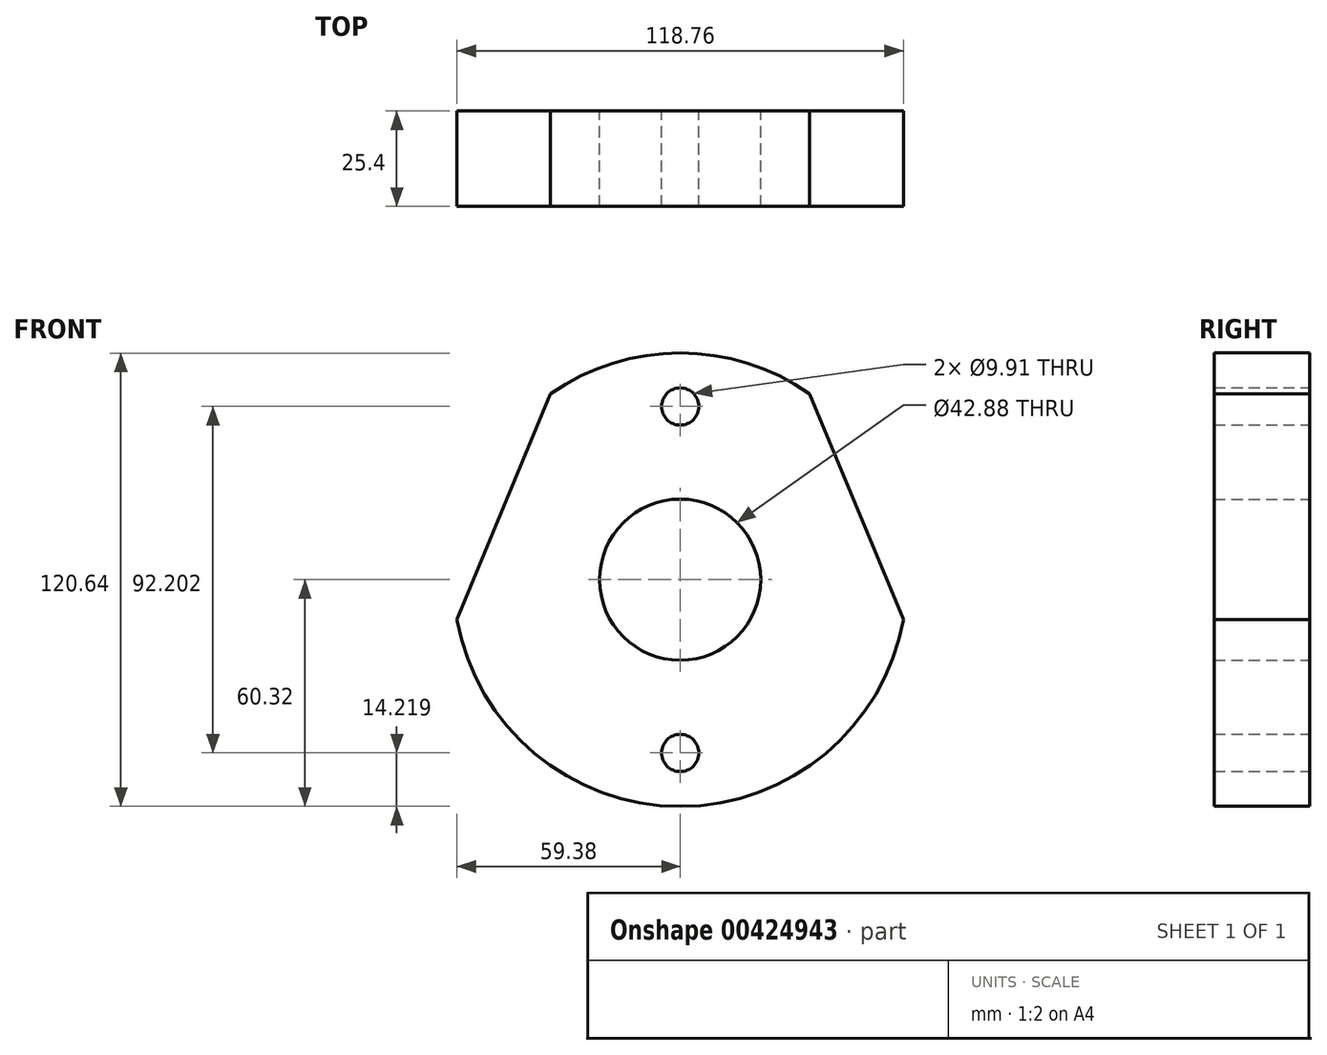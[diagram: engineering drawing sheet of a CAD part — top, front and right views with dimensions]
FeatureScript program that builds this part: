
annotation { "Feature Type Name" : "Feature", "Feature Type Description" : "" }
export const myFeature = defineFeature(function(context is Context, id is Id, definition is map)
    precondition{}
    {
        {
            var Q0;
            Q0=qCreatedBy(makeId("Front.planeOp"),FACE);
            var sketch = newSketch(context, id + "F0", { "sketchPlane" : qUnion([Q0])});
            skCircle(sketch, "E0", {"center": v(0, 0) * mm, "radius": 21.44 * mm});
            skCircle(sketch, "E1", {"center": v(0, 0) * mm, "radius": 60.33 * mm});
            skLineSegment(sketch, "E2", {"start": v(0, 0) * mm, "end": v(0, 69) * mm, "construction": true});
            skLineSegment(sketch, "E3", {"start": v(-34.48, 49.5) * mm, "end": v(-59.38, -10.62) * mm});
            skLineSegment(sketch, "E4.MirrorCS", {"start": v(34.48, 49.5) * mm, "end": v(59.38, -10.62) * mm});
            skCircle(sketch, "E5", {"center": v(0, 0) * mm, "radius": 50.8 * mm, "construction": true});
            skCircle(sketch, "E6", {"center": v(0, 46.1) * mm, "radius": 4.95 * mm});
            skLineSegment(sketch, "E7", {"start": v(0, 0) * mm, "end": v(-60.33, 0) * mm, "construction": true});
            skCircle(sketch, "E8.MirrorC", {"center": v(0, -46.1) * mm, "radius": 4.95 * mm});
            skSolve(sketch);
        }
        {
            var Q0;
            Q0=makeQuery(id+"F0.imprint","IMPRINT",FACE,{"disambiguationData":[TD([[makeQuery(id+"F0.imprint","IMPRINT",EDGE,{"derivedFrom":sQuery(id+"F0.wireOp",EDGE,"E0")}),-1.0]])]});
            extrude(context, id + "F1", {"entities" : qUnion([Q0]), "depth" : 25.4 * mm, "symmetric" : true});
        }
    });
